# Revit family: Haworth_Masters_Reception_StationU
name_source: partatom
category: Furniture Systems
revit_build: Autodesk Revit 2018 (Build: 20170223_1515(x64)
units: mm (PartAtom-declared; Revit-internal decimal feet)

## family parameters
Always vertical = Yes
Cut with Voids When Loaded = No
OmniClass Number = 23.40.70.14.64.21
OmniClass Title = Systems Furniture
Part Type = Normal
Room Calculation Point = No
Round Connector Dimension = Use Diameter
Shared = No
Work Plane-Based = No

## types (1)
- 74d 100w
    Actual Depth = 74 1/4"
    Actual Width = 100 1/2"
    Assembly Code = E2020200
    Bar Pull = No
    Bridge Panel Height = 43"
    Cabinet Finish = Haworth - Wood - Light Maple VP-LM
    Classic Pull = Yes
    Description = Haworth_Masters-Reception_Station_U
    Desk Depth = 29"
    Drawer Finish = Haworth - Wood - Light Maple VP-LM
    Front Finish = Haworth - Wood - Light Maple VP-LM
    LEED Data = http://www.haworth.com
    Linear Pull = No
    Manufacturer = Haworth
    Model = Haworth_Masters-Reception_Station_U
    Modesty Indent Width = 0"
    Panel Height = 43"
    Panel Thickness = 1 1/4"
    Panel Thickness Half = 5/8"
    Panel Width = 97 3/8"
    Pedestal Depth = 29"
    Product Page URL = http://www.haworth.com
    Pull Finish = Haworth - Metal - Satin Nickel
    Return Depth = 18"
    Revision Number = 1
    Size = Verify Final Dim. w/ Haworth
    Surface Thickness = 1 1/4"
    Surface Top = 29 5/16"
    Sustainability Info = http://www.haworth.com
    T Support Depth = 9"
    Transaction Depth = 12"
    Trim Finish = Haworth - Metal - Brushed Aluminum
    URL = www.haworth.com
    Warranty = http://www.haworth.com
    Worksurface Finish = Haworth - Wood - Light Maple VP-LM

## geometry (parser evidence)
native form markers: Blend x4, Sweep x15
no freeform markers — native parametric forms only
